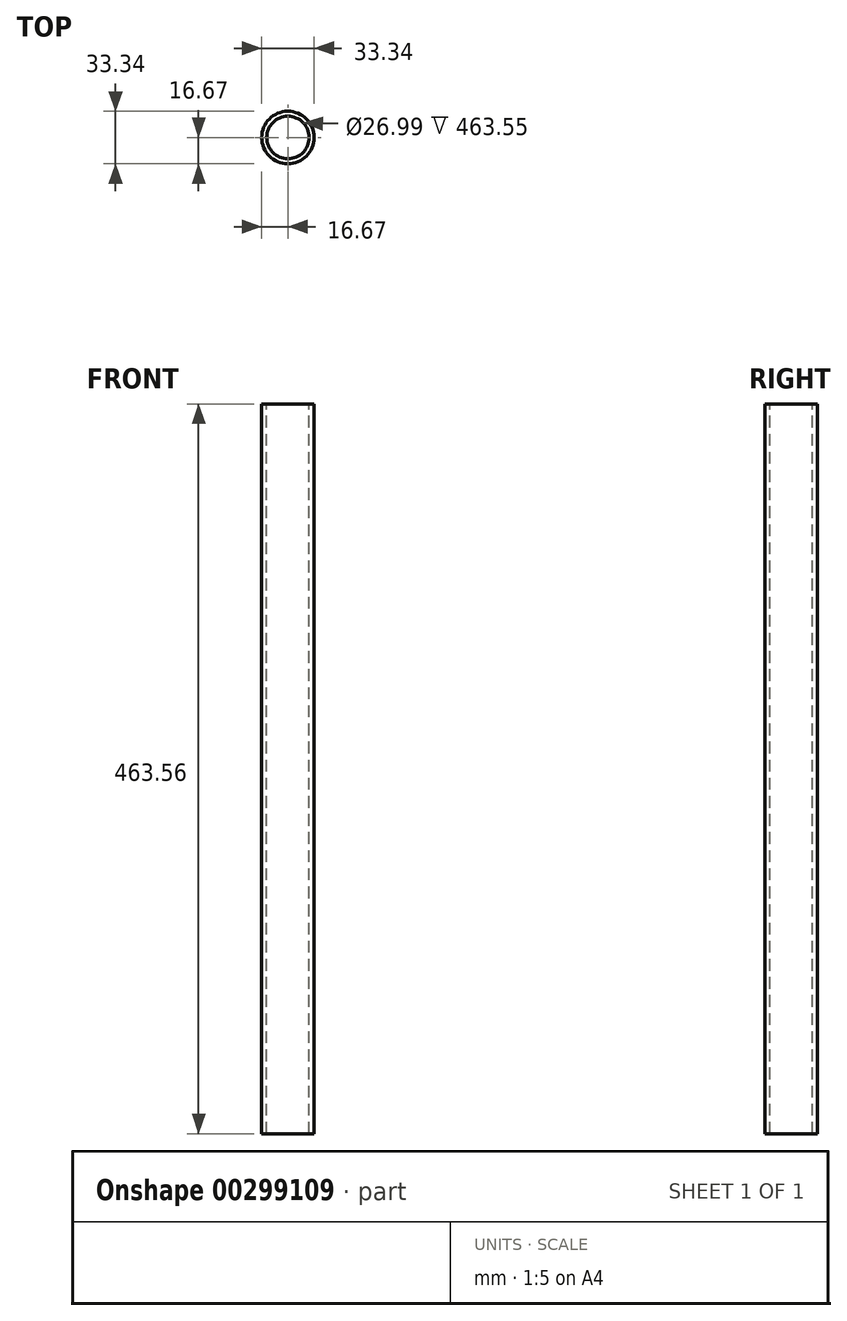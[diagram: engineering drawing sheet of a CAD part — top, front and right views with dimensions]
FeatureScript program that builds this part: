
annotation { "Feature Type Name" : "Feature", "Feature Type Description" : "" }
export const myFeature = defineFeature(function(context is Context, id is Id, definition is map)
    precondition{}
    {
        {
            var Q0;
            Q0=qCreatedBy(makeId("Top.planeOp"),FACE);
            var sketch = newSketch(context, id + "F0", { "sketchPlane" : qUnion([Q0])});
            skCircle(sketch, "E0", {"center": v(0, 0) * mm, "radius": 16.67 * mm});
            skSolve(sketch);
        }
        {
            var Q0;
            Q0 = qSketchRegion(id + "F0", true);
            extrude(context, id + "F1", {"entities" : qUnion([Q0]), "endBound" : BoundingType.SYMMETRIC, "depth" : 463.55 * mm});
        }
        {
            var Q0;
            Q0=makeQuery(id+"F1.opExtrude","CAP_FACE",FACE,{"disambiguationData":[OSD([sQuery(id+"F0.wireOp",EDGE,"E0")])],"isStart":false});
            var sketch = newSketch(context, id + "F2", { "sketchPlane" : qUnion([Q0])});
            skCircle(sketch, "E1", {"center": v(0, 0) * mm, "radius": 13.5 * mm});
            skSolve(sketch);
        }
        {
            var Q0;
            Q0 = qSketchRegion(id + "F2", true);
            extrude(context, id + "F3", {"entities" : qUnion([Q0]), "operationType" : NewBodyOperationType.REMOVE, "endBound" : BoundingType.THROUGH_ALL, "oppositeDirection" : true, "depth" : 25.4 * mm});
        }
    });
